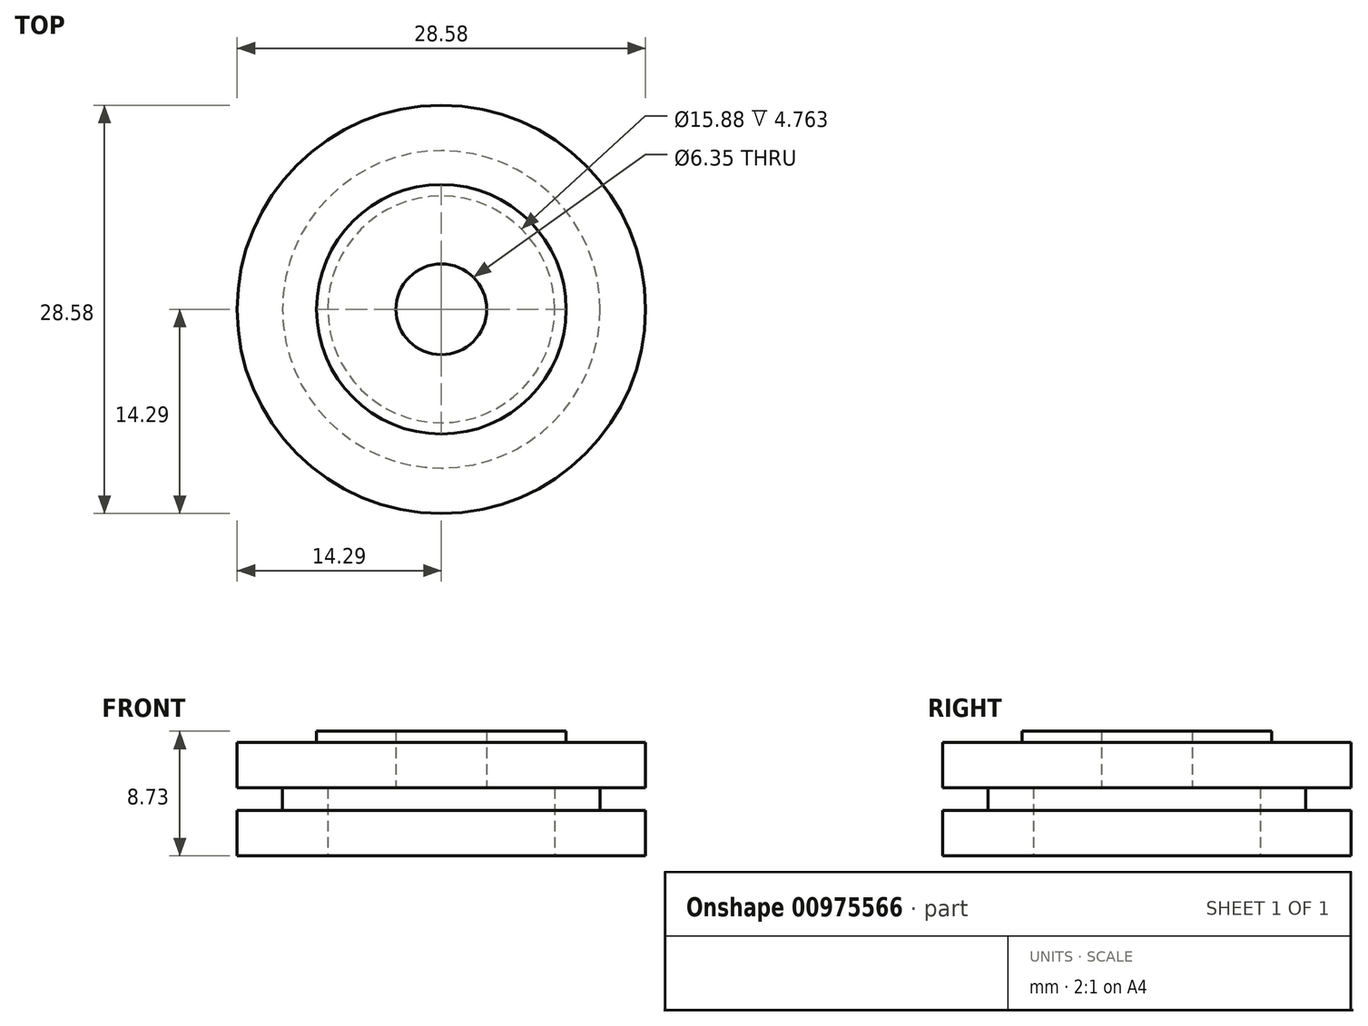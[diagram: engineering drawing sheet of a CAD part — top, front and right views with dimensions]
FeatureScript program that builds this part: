
annotation { "Feature Type Name" : "Feature", "Feature Type Description" : "" }
export const myFeature = defineFeature(function(context is Context, id is Id, definition is map)
    precondition{}
    {
        {
            var Q0;
            Q0=qCreatedBy(makeId("Front.planeOp"),FACE);
            var sketch = newSketch(context, id + "F0", { "sketchPlane" : qUnion([Q0])});
            skLineSegment(sketch, "E0", {"start": v(0, 0) * mm, "end": v(0, 21.81) * mm, "construction": true});
            skLineSegment(sketch, "E1", {"start": v(7.94, 5.08) * mm, "end": v(14.29, 5.08) * mm});
            skLineSegment(sketch, "E2", {"start": v(14.29, 5.08) * mm, "end": v(14.29, 8.26) * mm});
            skLineSegment(sketch, "E3", {"start": v(14.29, 8.26) * mm, "end": v(11.11, 8.26) * mm});
            skLineSegment(sketch, "E4", {"start": v(11.11, 8.26) * mm, "end": v(11.11, 9.85) * mm});
            skLineSegment(sketch, "E5", {"start": v(11.11, 9.85) * mm, "end": v(14.29, 9.85) * mm});
            skLineSegment(sketch, "E6", {"start": v(14.29, 9.85) * mm, "end": v(14.29, 13.02) * mm});
            skLineSegment(sketch, "E7", {"start": v(14.29, 13.02) * mm, "end": v(8.73, 13.02) * mm});
            skLineSegment(sketch, "E8", {"start": v(8.73, 13.02) * mm, "end": v(8.73, 13.81) * mm});
            skLineSegment(sketch, "E9", {"start": v(8.73, 13.81) * mm, "end": v(3.17, 13.81) * mm});
            skLineSegment(sketch, "E10", {"start": v(3.17, 13.81) * mm, "end": v(3.18, 9.85) * mm});
            skLineSegment(sketch, "E11", {"start": v(3.18, 9.85) * mm, "end": v(7.94, 9.85) * mm});
            skLineSegment(sketch, "E12", {"start": v(7.94, 9.85) * mm, "end": v(7.94, 5.08) * mm});
            skSolve(sketch);
        }
        {
            var Q0;
            Q0 = qSketchRegion(id + "F0", true);
            var Q1;
            Q1=sQuery(id+"F0.wireOp",EDGE,"E0");
            revolve(context, id + "F1", {"surfaceOperationType" : NewSurfaceOperationType.NEW, "entities" : qUnion([Q0]), "axis" : qUnion([Q1]), "revolveType" : RevolveType.FULL});
        }
    });
